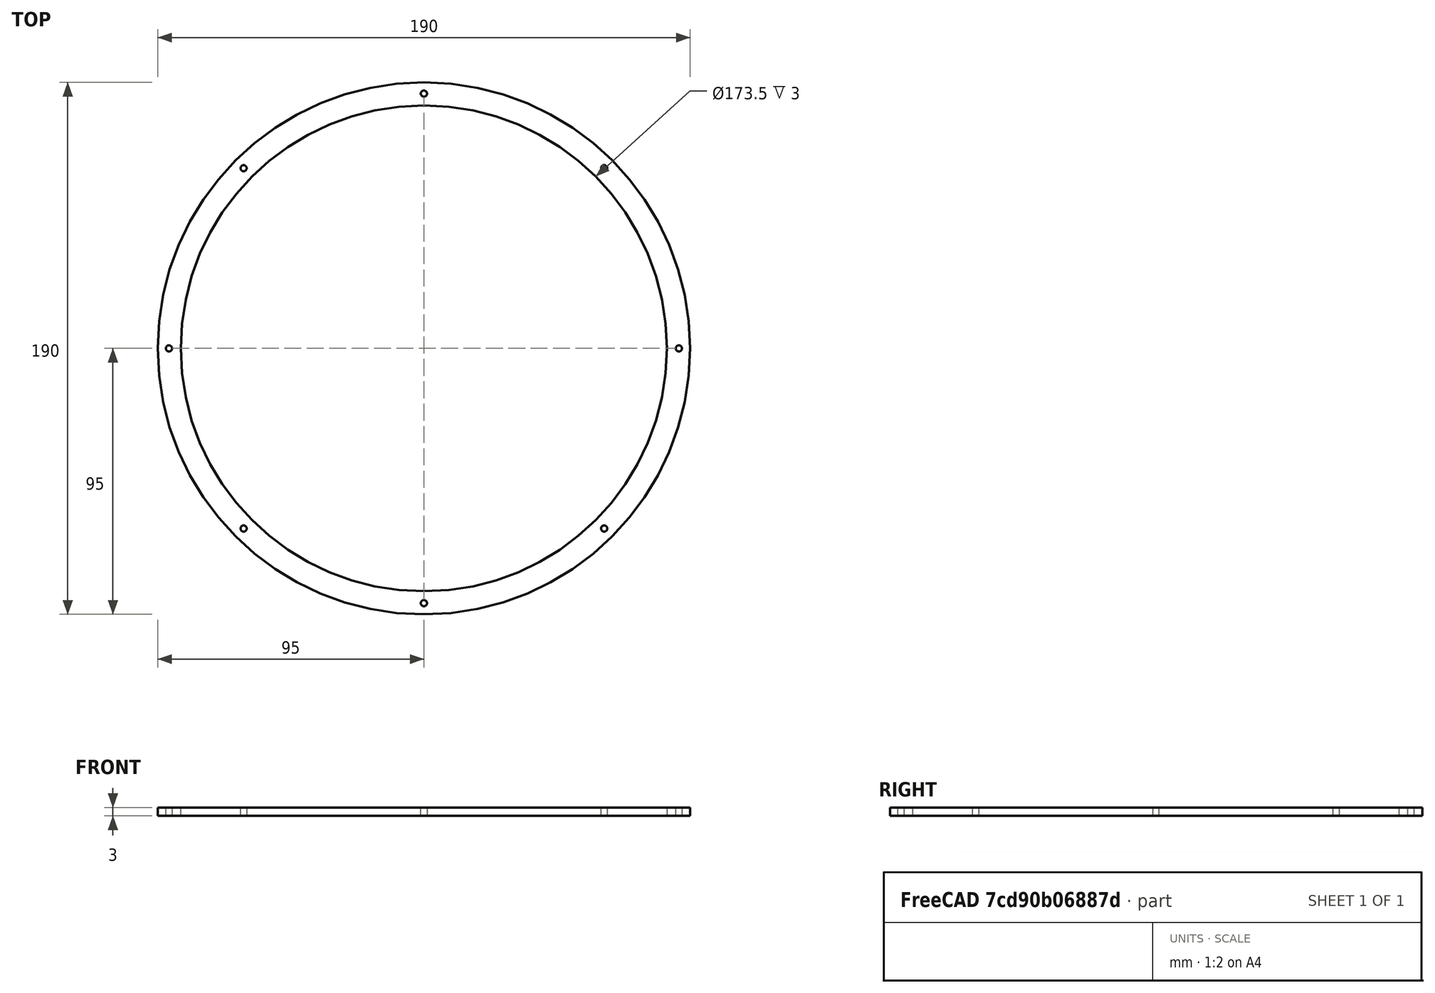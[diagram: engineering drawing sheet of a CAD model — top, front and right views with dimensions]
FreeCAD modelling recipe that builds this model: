
FCSTD DOCUMENT  (FreeCAD 0.19R24276 (Git))
Label: Out_gear_t176_d185_5_otv_bort_190_from_part_15_holder
License: All rights reserved
LicenseURL: http://en.wikipedia.org/wiki/All_rights_reserved
objects: Sketcher::SketchObject×2, PartDesign::Pad×1, PartDesign::Pocket×1, PartDesign::Body×1
note: 7 computed .brp shape members not serialized (recipe doc carries the construction recipe); baked Part::Feature solids carry a one-line shape summary decoded from their .brp

FEATURE [Sketcher::SketchObject] Sketch
  FullyConstrained = false
  MapMode = 5
  Support = -> [XY_Plane]
  sketch-geometry (17):
    g0: LineSegment StartX=0 StartY=0 StartZ=0 EndX=64.3467 EndY=64.3467 EndZ=0
    g1: Circle CenterX=0 CenterY=0 CenterZ=0 NormalX=0 NormalY=0 NormalZ=1 AngleXU=0 Radius=91
    g2: Circle CenterX=64.3467 CenterY=64.3467 CenterZ=0 NormalX=0 NormalY=0 NormalZ=1 AngleXU=0 Radius=1.1
    g3: LineSegment StartX=0 StartY=0 StartZ=0 EndX=-1.5e-15 EndY=91 EndZ=0
    g4: LineSegment StartX=0 StartY=0 StartZ=0 EndX=91 EndY=0 EndZ=0
    g5: Circle CenterX=-1.5e-15 CenterY=91 CenterZ=0 NormalX=0 NormalY=0 NormalZ=1 AngleXU=0 Radius=1.1
    g6: Circle CenterX=91 CenterY=0 CenterZ=0 NormalX=0 NormalY=0 NormalZ=1 AngleXU=0 Radius=1.1
    g7: Circle CenterX=64.3467 CenterY=-64.3467 CenterZ=0 NormalX=0 NormalY=0 NormalZ=1 AngleXU=0 Radius=1.1
    g8: Circle CenterX=-1.5e-15 CenterY=-91 CenterZ=0 NormalX=0 NormalY=0 NormalZ=1 AngleXU=0 Radius=1.1
    g9: LineSegment StartX=0 StartY=0 StartZ=0 EndX=-1.5e-15 EndY=-91 EndZ=0
    g10: LineSegment StartX=0 StartY=0 StartZ=0 EndX=64.3467 EndY=-64.3467 EndZ=0
    g11: LineSegment StartX=0 StartY=0 StartZ=0 EndX=-64.3467 EndY=-64.3467 EndZ=0
    g12: LineSegment StartX=0 StartY=0 StartZ=0 EndX=-91 EndY=0 EndZ=0
    g13: LineSegment StartX=0 StartY=0 StartZ=0 EndX=-64.3467 EndY=64.3467 EndZ=0
    g14: Circle CenterX=-91 CenterY=0 CenterZ=0 NormalX=0 NormalY=0 NormalZ=1 AngleXU=0 Radius=1.1
    g15: Circle CenterX=-64.3467 CenterY=-64.3467 CenterZ=0 NormalX=0 NormalY=0 NormalZ=1 AngleXU=0 Radius=1.1
    g16: Circle CenterX=-64.3467 CenterY=64.3467 CenterZ=0 NormalX=0 NormalY=0 NormalZ=1 AngleXU=0 Radius=1.1
  constraints (26):
    c: Coincident(g0,g-1)
    c: Coincident(g1,g-1)
    c: Diameter(g1) = 182
    c: PointOnObject(g0,g1)
    c: Coincident(g2,g0)
    c: Diameter(g2) = 2.2
    c: Coincident(g3,g-1)
    c: Coincident(g4,g-1)
    c: PointOnObject(g4,g1)
    c: PointOnObject(g3,g1)
    c: Coincident(g5,g3)
    c: Coincident(g6,g4)
    c: Equal(g6,g2)
    c: Equal(g2,g5)
    c: Angle(g4,g-1) = 0
    c: Angle(g-1,g0) = 0.785398
    c: Angle(g0,g3) = 0.785398
    c: Coincident(g7,g10)
    c: Diameter(g7) = 2.2
    c: Coincident(g8,g9)
    c: Equal(g7,g8)
    c: Angle(g10,g9) = -0.785398
    c: Coincident(g14,g12)
    c: Coincident(g15,g11)
    c: Diameter(g15) = 2.2
    c: Diameter(g16) = 2.2
FEATURE [Sketcher::SketchObject] Sketch001
  FullyConstrained = true
  MapMode = 5
  Placement = pos=(0,0,0) rot=(1,0,0;3.14159rad)
  sketch-geometry (2):
    g0: Circle CenterX=0 CenterY=0 CenterZ=0 NormalX=0 NormalY=0 NormalZ=1 AngleXU=0 Radius=95
    g1: Circle CenterX=0 CenterY=0 CenterZ=0 NormalX=0 NormalY=0 NormalZ=1 AngleXU=0 Radius=86.75
  constraints (4):
    c: Coincident(g0,g-1)
    c: Diameter(g0) = 190
    c: Coincident(g1,g0)
    c: Diameter(g1) = 173.5
FEATURE [PartDesign::Pad] Pad
  Direction = (1,1,1)
  Length = 3
  Length2 = 100
  Placement = pos=(0,0,0) rot=(1,0,0;3.14159rad)
  Profile = -> Sketch001
  Type = 0
FEATURE [PartDesign::Pocket] Pocket
  BaseFeature = -> Pad
  Length = 5
  Length2 = 100
  Midplane = true
  Placement = pos=(0,0,0) rot=(1,0,0;3.14159rad)
  Profile = -> Sketch
  Type = 1
FEATURE [PartDesign::Body] Body
  Group = -> [Sketch001,Pad,Sketch,Pocket]
  Origin = -> Origin
  Tip = -> Pocket
